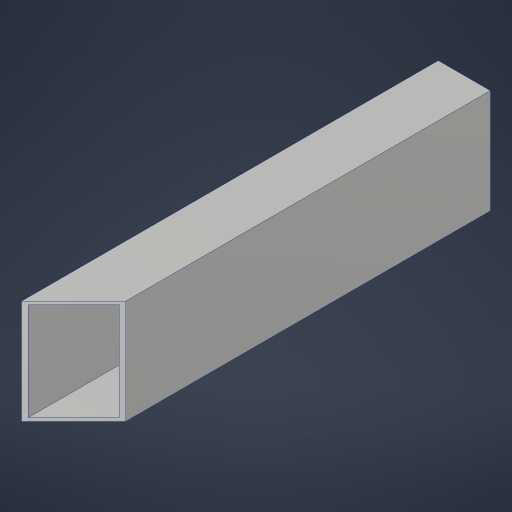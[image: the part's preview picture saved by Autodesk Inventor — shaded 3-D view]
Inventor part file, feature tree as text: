
AUTODESK INVENTOR PART (.ipt)
format: ipt  version: 2023.4 (Build 274418000, 418)  size: 170,496 bytes
history: native  units: in
note: dims shown in document units (in); Inventor stores cm internally (conversion verified against a paired STEP export)
features: extrude x2, sketch x1, projected_geometry x1
ambient origin geometry x8: Origin, YZ Plane, XZ Plane, XY Plane, X Axis, Y Axis, Z Axis, Center Point
bodies: Solid1 (feature_tree)
feature tree (4):
  extrude  "Extrusion1"  TaperAngle=45.0deg  [1 undecoded]
  extrude  "Extrusion4"  TaperAngle=0.0deg  [1 undecoded]
  sketch  "Sketch4"  dims[d4=0.0in d13=45.0deg d14=0.0in d15=0.0in]
  projected_geometry  "Project Cut Edges1"
note: 2 required parameter values undecoded (feature->parameter linkage not recoverable at this tier; creation-order binding heuristic only, values carry confidence <= 0.55)
